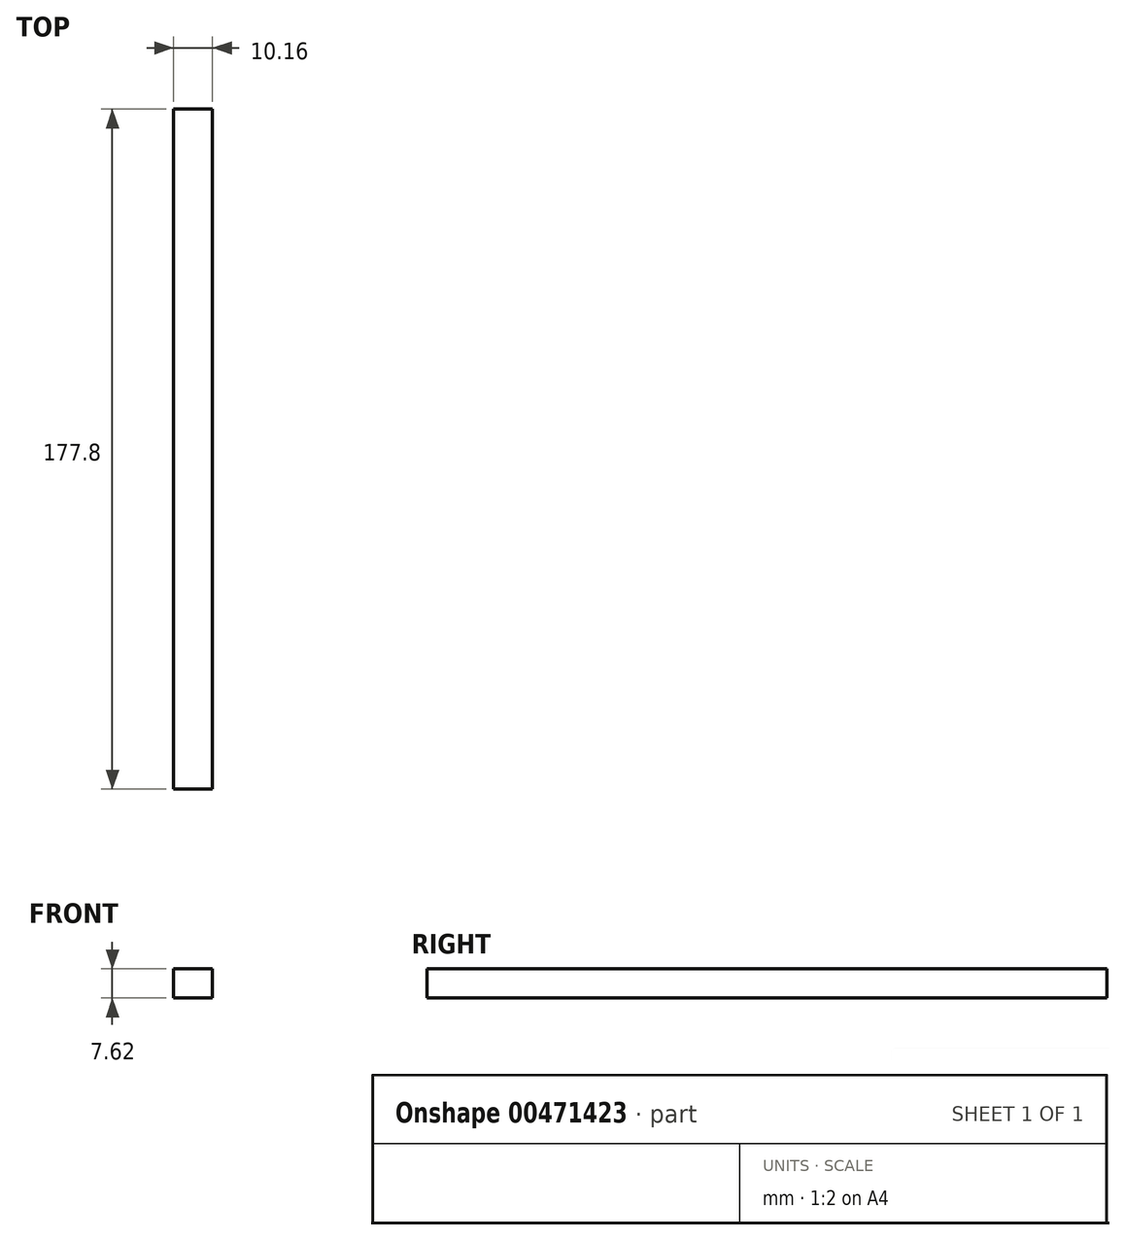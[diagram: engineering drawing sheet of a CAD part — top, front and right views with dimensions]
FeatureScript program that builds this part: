
annotation { "Feature Type Name" : "Feature", "Feature Type Description" : "" }
export const myFeature = defineFeature(function(context is Context, id is Id, definition is map)
    precondition{}
    {
        {
            var Q0;
            Q0=qCreatedBy(makeId("Front.planeOp"),FACE);
            var sketch = newSketch(context, id + "F0", { "sketchPlane" : qUnion([Q0])});
            skLineSegment(sketch, "E0.bottom", {"start": v(0, 0) * mm, "end": v(-10.16, 0) * mm});
            skLineSegment(sketch, "E0.top", {"start": v(0, 7.62) * mm, "end": v(-10.16, 7.62) * mm});
            skLineSegment(sketch, "E0.left", {"start": v(0, 0) * mm, "end": v(0, 7.62) * mm});
            skLineSegment(sketch, "E0.right", {"start": v(-10.16, 0) * mm, "end": v(-10.16, 7.62) * mm});
            skSolve(sketch);
        }
        {
            var Q0;
            Q0 = qSketchRegion(id + "F0", true);
            extrude(context, id + "F1", {"entities" : qUnion([Q0]), "depth" : 177.8 * mm});
        }
    });
